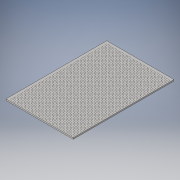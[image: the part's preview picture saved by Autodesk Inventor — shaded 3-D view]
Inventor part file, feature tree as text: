
AUTODESK INVENTOR PART (.ipt)
format: ipt  version: 2016 (Build 200138000, 138)  size: 2,598,912 bytes
history: native  units: in
note: dims shown in document units (in); Inventor stores cm internally (conversion verified against a paired STEP export)
features: sketch x2, extrude x1, hole x1, pattern_linear x1
ambient origin geometry x8: Origin, YZ Plane, XZ Plane, XY Plane, X Axis, Y Axis, Z Axis, Center Point
bodies: Solid1 (feature_tree)
feature tree (5):
  extrude  "Extrusion1"  Depth=48.0in
  hole  "Hole1"  [1 undecoded]
  pattern_linear  "Rectangular Pattern1"  Spacing1=1.0in  [1 undecoded]
  sketch  "Sketch1"  dims[d0=72.0in d1=48.0in]
  sketch  "Sketch2"  dims[d2=1.0in d3=0.0in d4=1.0in d5=1.0in d6=0.196in d7=0.5in d8=0.375in d9=0.25in d10=0.5635in d11=1.0in d12=0.8108in d13=18.1102in d15=1.0in d16=27.5591in d18=1.0in]
note: 2 required parameter values undecoded (feature->parameter linkage not recoverable at this tier; creation-order binding heuristic only, values carry confidence <= 0.55)
